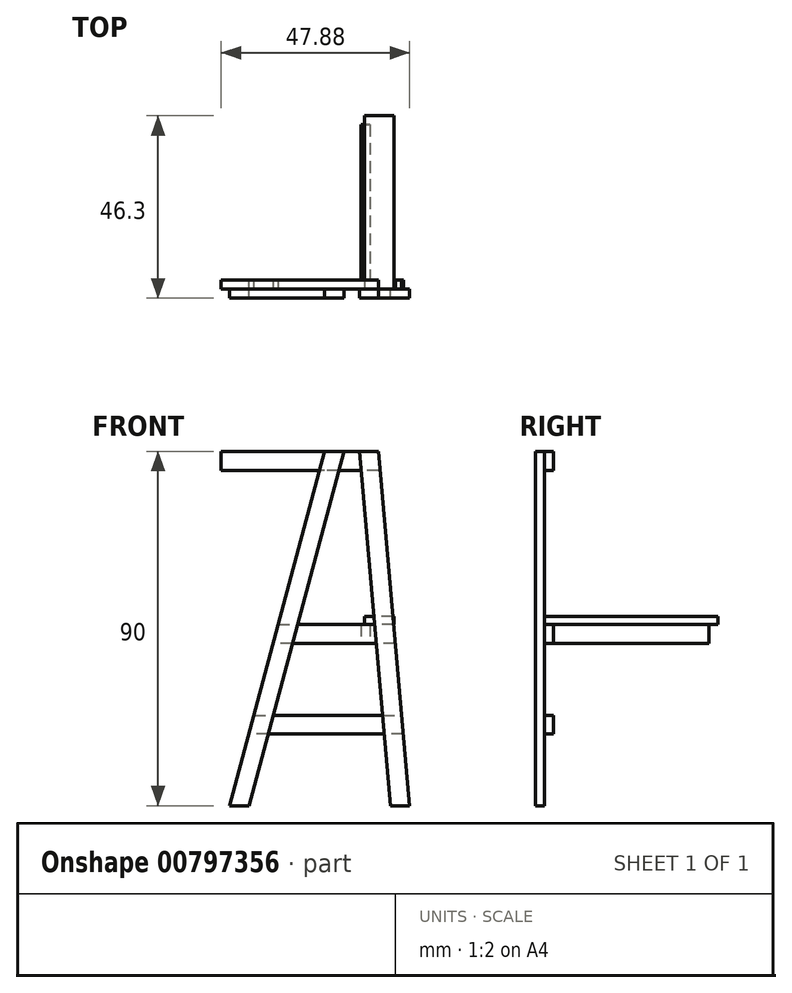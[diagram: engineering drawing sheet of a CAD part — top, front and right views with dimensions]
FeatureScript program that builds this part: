
annotation { "Feature Type Name" : "Feature", "Feature Type Description" : "" }
export const myFeature = defineFeature(function(context is Context, id is Id, definition is map)
    precondition{}
    {
        {
            var Q0;
            Q0=qCreatedBy(makeId("Front.planeOp"),FACE);
            var sketch = newSketch(context, id + "F0", { "sketchPlane" : qUnion([Q0])});
            skLineSegment(sketch, "E0.bottom", {"start": v(10, 0) * mm, "end": v(14.82, 0) * mm});
            skLineSegment(sketch, "E0.top", {"start": v(6.94, 90) * mm, "end": v(2.13, 90) * mm});
            skLineSegment(sketch, "E0.left", {"start": v(14.82, 0) * mm, "end": v(6.94, 90) * mm});
            skLineSegment(sketch, "E0.right", {"start": v(10, 0) * mm, "end": v(2.13, 90) * mm});
            skLineSegment(sketch, "E1", {"start": v(-26, 0) * mm, "end": v(-1.88, 90) * mm});
            skLineSegment(sketch, "E2", {"start": v(-1.88, 90) * mm, "end": v(-6.85, 90) * mm});
            skLineSegment(sketch, "E3", {"start": v(-6.85, 90) * mm, "end": v(-30.97, 0) * mm});
            skLineSegment(sketch, "E4", {"start": v(-30.97, 0) * mm, "end": v(-26, 0) * mm});
            skSolve(sketch);
        }
        {
            var Q0;
            Q0 = qSketchRegion(id + "F0", true);
            extrude(context, id + "F1", {"entities" : qUnion([Q0]), "depth" : 2.3 * mm, "offsetDistance" : 25 * mm});
        }
        {
            var Q0;
            Q0=makeQuery(id+"F1.opExtrude","CAP_FACE",FACE,{"disambiguationData":[OSD([sQuery(id+"F0.wireOp",EDGE,"E0.bottom"),sQuery(id+"F0.wireOp",EDGE,"E0.top"),sQuery(id+"F0.wireOp",EDGE,"E0.left"),sQuery(id+"F0.wireOp",EDGE,"E0.right")])],"isStart":true});
            var sketch = newSketch(context, id + "F2", { "sketchPlane" : qUnion([Q0])});
            skLineSegment(sketch, "E5", {"start": v(-13.23, 18.2) * mm, "end": v(26.1, 18.2) * mm});
            skLineSegment(sketch, "E6", {"start": v(26.1, 18.2) * mm, "end": v(24.8, 23) * mm});
            skLineSegment(sketch, "E7", {"start": v(24.8, 23) * mm, "end": v(-12.8, 23) * mm});
            skLineSegment(sketch, "E8", {"start": v(-12.8, 23) * mm, "end": v(-13.23, 18.2) * mm});
            skLineSegment(sketch, "E9", {"start": v(-11.21, 41.2) * mm, "end": v(19.93, 41.2) * mm});
            skLineSegment(sketch, "E10", {"start": v(18.64, 46) * mm, "end": v(-10.8, 46) * mm});
            skLineSegment(sketch, "E11", {"start": v(-10.8, 46) * mm, "end": v(-11.21, 41.2) * mm});
            skLineSegment(sketch, "E12", {"start": v(18.64, 46) * mm, "end": v(19.93, 41.2) * mm});
            skLineSegment(sketch, "E13.bottom", {"start": v(-6.94, 90) * mm, "end": v(33.06, 90) * mm});
            skLineSegment(sketch, "E13.top", {"start": v(-6.94, 85.2) * mm, "end": v(33.06, 85.2) * mm});
            skLineSegment(sketch, "E13.left", {"start": v(-6.94, 90) * mm, "end": v(-6.94, 85.2) * mm});
            skLineSegment(sketch, "E13.right", {"start": v(33.06, 90) * mm, "end": v(33.06, 85.2) * mm});
            skSolve(sketch);
        }
        {
            var Q0;
            Q0 = qSketchRegion(id + "F2", true);
            extrude(context, id + "F3", {"entities" : qUnion([Q0]), "depth" : 2.3 * mm, "offsetDistance" : 25 * mm});
        }
        {
            var Q0;
            Q0=makeQuery(id+"F1.opExtrude","CAP_FACE",FACE,{"disambiguationData":[OSD([sQuery(id+"F0.wireOp",EDGE,"E0.bottom"),sQuery(id+"F0.wireOp",EDGE,"E0.top"),sQuery(id+"F0.wireOp",EDGE,"E0.left"),sQuery(id+"F0.wireOp",EDGE,"E0.right")])],"isStart":true});
            var sketch = newSketch(context, id + "F4", { "sketchPlane" : qUnion([Q0])});
            skLineSegment(sketch, "E14.bottom", {"start": v(-10.8, 46) * mm, "end": v(-3.3, 46) * mm});
            skLineSegment(sketch, "E14.top", {"start": v(-10.8, 48.1) * mm, "end": v(-3.3, 48.1) * mm});
            skLineSegment(sketch, "E14.left", {"start": v(-10.8, 46) * mm, "end": v(-10.8, 48.1) * mm});
            skLineSegment(sketch, "E14.right", {"start": v(-3.3, 46) * mm, "end": v(-3.3, 48.1) * mm});
            skSolve(sketch);
        }
        {
            var Q0;
            Q0 = qSketchRegion(id + "F4", true);
            extrude(context, id + "F5", {"entities" : qUnion([Q0]), "depth" : 44 * mm, "offsetDistance" : 25 * mm});
        }
        {
            var Q0;
            Q0=makeQuery(id+"F3.opExtrude","CAP_FACE",FACE,{"disambiguationData":[OSD([sQuery(id+"F2.wireOp",EDGE,"E9"),sQuery(id+"F2.wireOp",EDGE,"E10"),sQuery(id+"F2.wireOp",EDGE,"E11"),sQuery(id+"F2.wireOp",EDGE,"E12")])],"isStart":false});
            var sketch = newSketch(context, id + "F6", { "sketchPlane" : qUnion([Q0])});
            skLineSegment(sketch, "E15.bottom", {"start": v(-2.48, 46) * mm, "end": v(-4.78, 46) * mm});
            skLineSegment(sketch, "E15.top", {"start": v(-2.48, 41.2) * mm, "end": v(-4.78, 41.2) * mm});
            skLineSegment(sketch, "E15.left", {"start": v(-2.48, 46) * mm, "end": v(-2.48, 41.2) * mm});
            skLineSegment(sketch, "E15.right", {"start": v(-4.78, 46) * mm, "end": v(-4.78, 41.2) * mm});
            skSolve(sketch);
        }
        {
            var Q0;
            Q0 = qSketchRegion(id + "F6", true);
            extrude(context, id + "F7", {"entities" : qUnion([Q0]), "depth" : (44 - 2 * 2.3) * mm, "offsetDistance" : 25 * mm});
        }
    });
